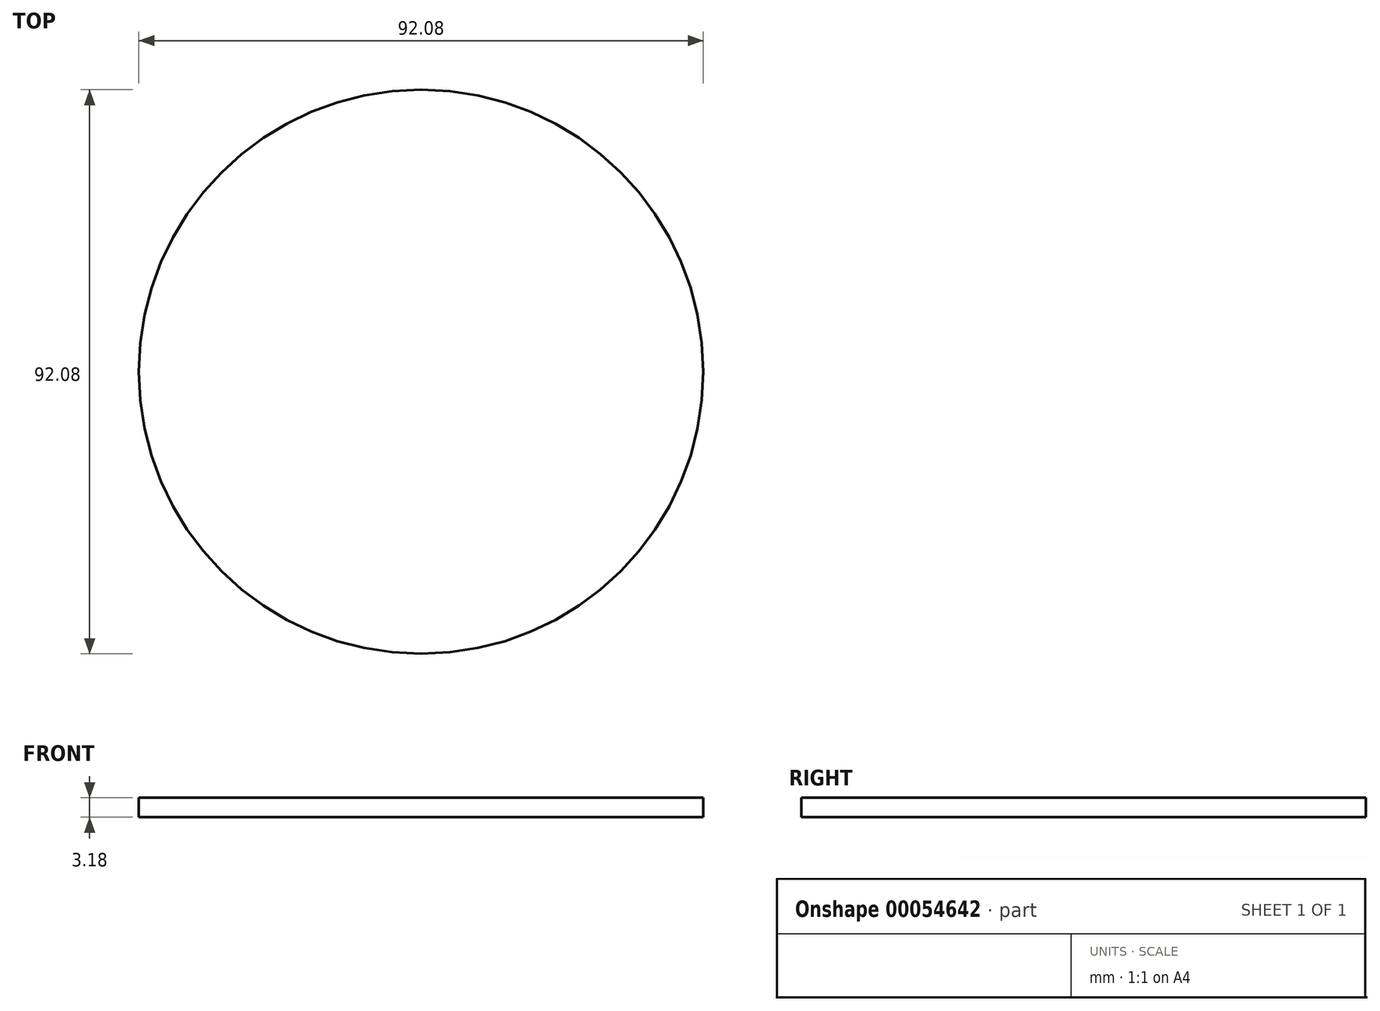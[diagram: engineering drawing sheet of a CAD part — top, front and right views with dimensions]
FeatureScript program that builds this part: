
annotation { "Feature Type Name" : "Feature", "Feature Type Description" : "" }
export const myFeature = defineFeature(function(context is Context, id is Id, definition is map)
    precondition{}
    {
        {
            var Q0;
            Q0=qCreatedBy(makeId("Top.planeOp"),FACE);
            var sketch = newSketch(context, id + "F0", { "sketchPlane" : qUnion([Q0])});
            skCircle(sketch, "E0", {"center": v(0, 0) * mm, "radius": 46.04 * mm});
            skSolve(sketch);
        }
        {
            var Q0;
            Q0=makeQuery(id+"F0.imprint","IMPRINT",FACE,{"disambiguationData":[TD([[makeQuery(id+"F0.imprint","IMPRINT",EDGE,{"derivedFrom":sQuery(id+"F0.wireOp",EDGE,"E0")}),1.0]])]});
            extrude(context, id + "F1", {"entities" : qUnion([Q0]), "depth" : 3.17 * mm});
        }
    });
